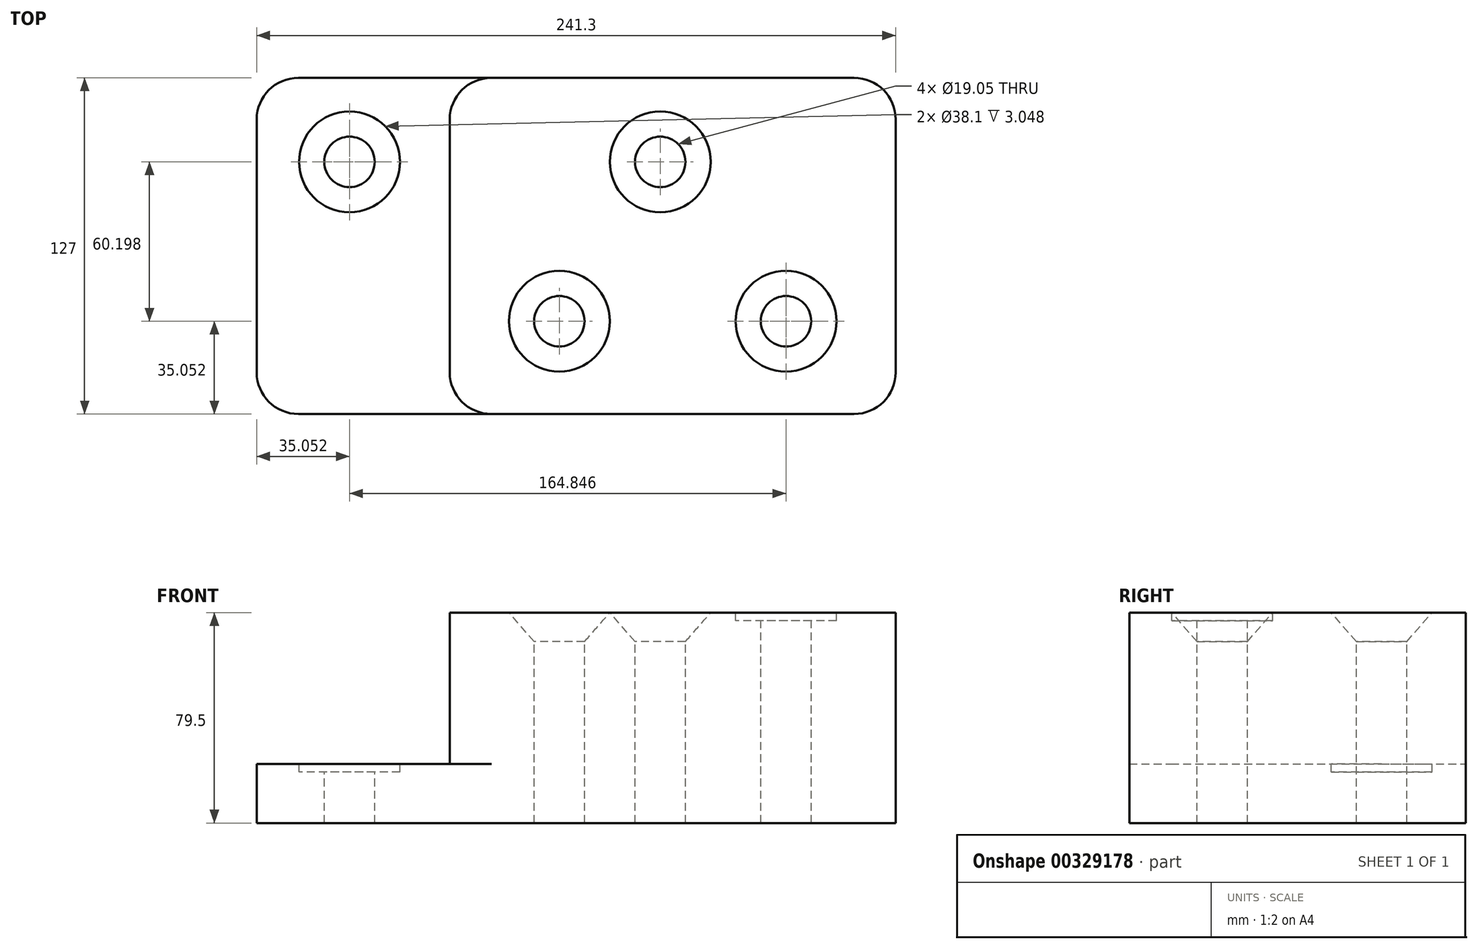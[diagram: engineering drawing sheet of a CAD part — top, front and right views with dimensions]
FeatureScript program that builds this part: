
annotation { "Feature Type Name" : "Feature", "Feature Type Description" : "" }
export const myFeature = defineFeature(function(context is Context, id is Id, definition is map)
    precondition{}
    {
        {
            var Q0;
            Q0=qCreatedBy(makeId("Front.planeOp"),FACE);
            var sketch = newSketch(context, id + "F0", { "sketchPlane" : qUnion([Q0])});
            skLineSegment(sketch, "E0", {"start": v(0, 0) * mm, "end": v(241.3, 0) * mm});
            skLineSegment(sketch, "E1", {"start": v(241.3, 0) * mm, "end": v(241.3, 79.5) * mm});
            skLineSegment(sketch, "E2", {"start": v(241.3, 79.5) * mm, "end": v(72.9, 79.5) * mm});
            skLineSegment(sketch, "E3", {"start": v(72.9, 79.5) * mm, "end": v(72.9, 22.35) * mm});
            skLineSegment(sketch, "E4", {"start": v(72.9, 22.35) * mm, "end": v(0, 22.35) * mm});
            skLineSegment(sketch, "E5", {"start": v(0, 22.35) * mm, "end": v(0, 0) * mm});
            skSolve(sketch);
        }
        {
            var Q0;
            Q0 = qSketchRegion(id + "F0", true);
            extrude(context, id + "F1", {"entities" : qUnion([Q0]), "depth" : 127 * mm});
        }
        {
            var Q0;
            Q0=makeQuery(id+"F1.opExtrude","CAP_EDGE",EDGE,{"disambiguationData":[OSD([sQuery(id+"F0.wireOp",EDGE,"E3")])],"isStart":false});
            var Q1;
            Q1=makeQuery(id+"F1.opExtrude","CAP_EDGE",EDGE,{"disambiguationData":[OSD([sQuery(id+"F0.wireOp",EDGE,"E3")])],"isStart":true});
            var Q2;
            Q2=makeQuery(id+"F1.opExtrude","CAP_EDGE",EDGE,{"disambiguationData":[OSD([sQuery(id+"F0.wireOp",EDGE,"E5")])],"isStart":true});
            var Q3;
            Q3=makeQuery(id+"F1.opExtrude","CAP_EDGE",EDGE,{"disambiguationData":[OSD([sQuery(id+"F0.wireOp",EDGE,"E5")])],"isStart":false});
            var Q4;
            Q4=makeQuery(id+"F1.opExtrude","CAP_EDGE",EDGE,{"disambiguationData":[OSD([sQuery(id+"F0.wireOp",EDGE,"E1")])],"isStart":false});
            var Q5;
            Q5=makeQuery(id+"F1.opExtrude","CAP_EDGE",EDGE,{"disambiguationData":[OSD([sQuery(id+"F0.wireOp",EDGE,"E1")])],"isStart":true});
            fillet(context, id + "F2", {"entities" : qUnion([Q0, Q1, Q2, Q3, Q4, Q5]), "radius" : 15.75 * mm, "tangentPropagation" : true, "allowEdgeOverflow" : false});
        }
        {
            var Q0;
            Q0=makeQuery(id+"F1.opExtrude","SWEPT_FACE",FACE,{"disambiguationData":[OSD([sQuery(id+"F0.wireOp",EDGE,"E2")])]});
            var sketch = newSketch(context, id + "F3", { "sketchPlane" : qUnion([Q0])});
            skPoint(sketch, "E6", {"position": v(35.05, -31.75) * mm});
            skPoint(sketch, "E7", {"position": v(152.4, -31.75) * mm});
            skPoint(sketch, "E8", {"position": v(114.3, -91.95) * mm});
            skPoint(sketch, "E9", {"position": v(199.9, -91.95) * mm});
            skSolve(sketch);
        }
        {
            var Q0;
            Q0=sQuery(id+"F3.wireOp",VERTEX,"E8");
            var Q1;
            Q1=sQuery(id+"F3.wireOp",VERTEX,"E7");
            var Q2;
            Q2=makeQuery(id+"F1.opExtrude","SWEPT_BODY",BODY,{"disambiguationData":[OSD([sQuery(id+"F0.wireOp",EDGE,"E0"),sQuery(id+"F0.wireOp",EDGE,"E1"),sQuery(id+"F0.wireOp",EDGE,"E2"),sQuery(id+"F0.wireOp",EDGE,"E3"),sQuery(id+"F0.wireOp",EDGE,"E4"),sQuery(id+"F0.wireOp",EDGE,"E5")])]});
            hole(context, id + "F4", {"style" : HoleStyle.C_SINK, "endStyle" : HoleEndStyle.THROUGH, "holeDiameter" : 19.05 * mm, "cSinkDiameter" : 38.1 * mm, "cSinkAngle" : 82 * degree, "tappedDepth" : 12.7 * mm, "tapClearance" : 3, "locations" : qUnion([Q0, Q1]), "scope" : qUnion([Q2])});
        }
        {
            var Q0;
            Q0=sQuery(id+"F3.wireOp",VERTEX,"E6");
            var Q1;
            Q1=sQuery(id+"F3.wireOp",VERTEX,"E9");
            var Q2;
            Q2=makeQuery(id+"F1.opExtrude","SWEPT_BODY",BODY,{"disambiguationData":[OSD([sQuery(id+"F0.wireOp",EDGE,"E0"),sQuery(id+"F0.wireOp",EDGE,"E1"),sQuery(id+"F0.wireOp",EDGE,"E2"),sQuery(id+"F0.wireOp",EDGE,"E3"),sQuery(id+"F0.wireOp",EDGE,"E4"),sQuery(id+"F0.wireOp",EDGE,"E5")])]});
            hole(context, id + "F5", {"style" : HoleStyle.C_BORE, "endStyle" : HoleEndStyle.THROUGH, "holeDiameter" : 19.05 * mm, "cBoreDiameter" : 38.1 * mm, "cBoreDepth" : 3.05 * mm, "tappedDepth" : 12.7 * mm, "tapClearance" : 3, "locations" : qUnion([Q0, Q1]), "scope" : qUnion([Q2])});
        }
    });
